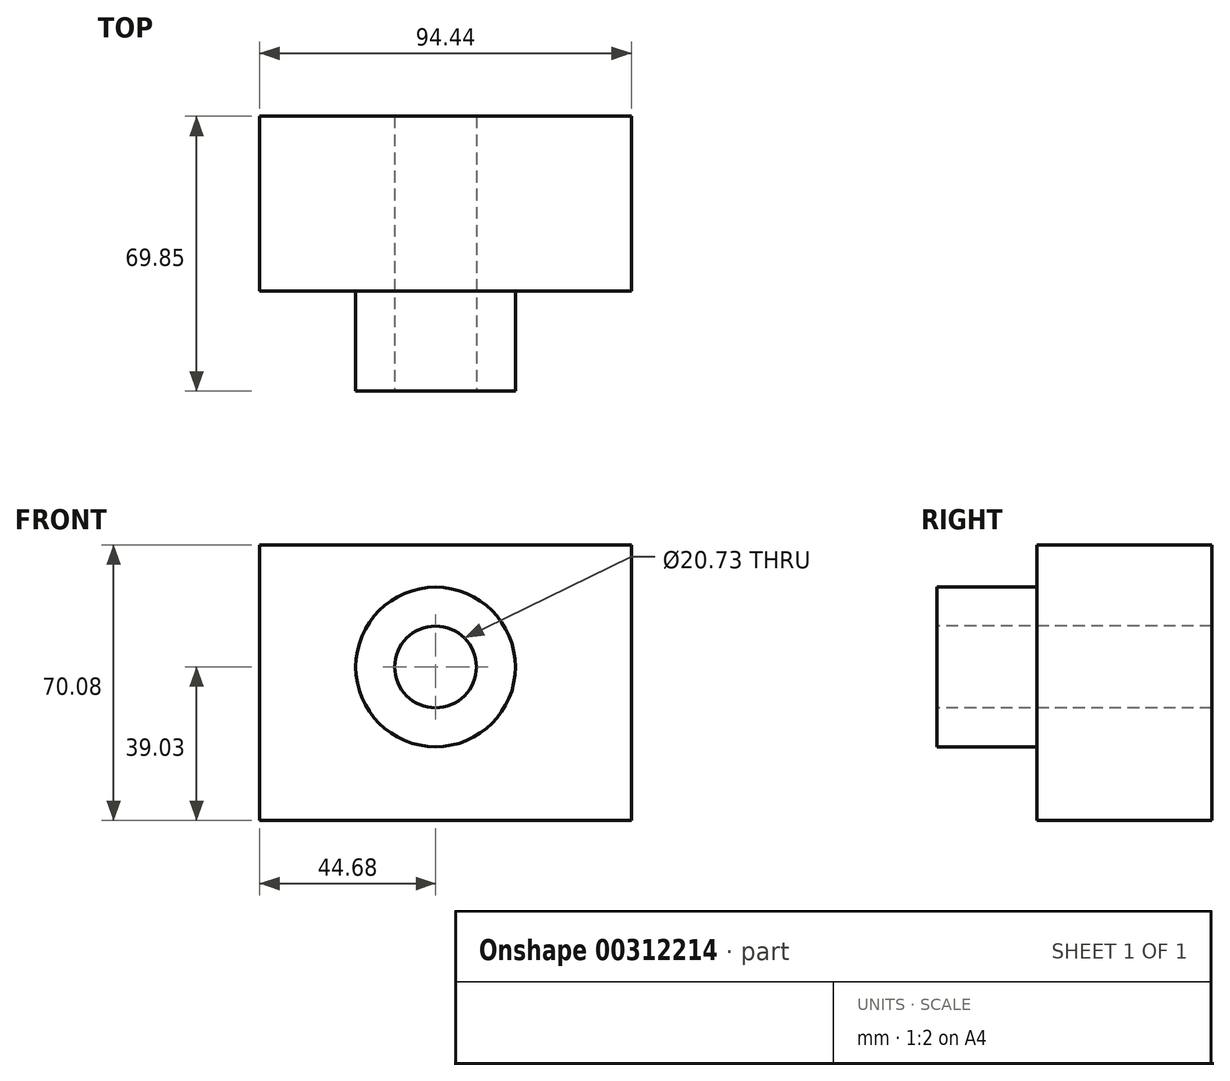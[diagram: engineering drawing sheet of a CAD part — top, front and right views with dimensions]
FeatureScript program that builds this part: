
annotation { "Feature Type Name" : "Feature", "Feature Type Description" : "" }
export const myFeature = defineFeature(function(context is Context, id is Id, definition is map)
    precondition{}
    {
        {
            var Q0;
            Q0=qCreatedBy(makeId("Front.planeOp"),FACE);
            var sketch = newSketch(context, id + "F0", { "sketchPlane" : qUnion([Q0])});
            skLineSegment(sketch, "E0.bottom", {"start": v(-44.68, 31.05) * mm, "end": v(49.76, 31.05) * mm});
            skLineSegment(sketch, "E0.top", {"start": v(-44.68, -39.03) * mm, "end": v(49.76, -39.03) * mm});
            skLineSegment(sketch, "E0.left", {"start": v(-44.68, 31.05) * mm, "end": v(-44.68, -39.03) * mm});
            skLineSegment(sketch, "E0.right", {"start": v(49.76, 31.05) * mm, "end": v(49.76, -39.03) * mm});
            skSolve(sketch);
        }
        {
            var Q0;
            Q0 = qSketchRegion(id + "F0", true);
            extrude(context, id + "F1", {"entities" : qUnion([Q0]), "depth" : 44.45 * mm});
        }
        {
            var Q0;
            Q0=makeQuery(id+"F1.opExtrude","CAP_FACE",FACE,{"disambiguationData":[OSD([sQuery(id+"F0.wireOp",EDGE,"E0.bottom"),sQuery(id+"F0.wireOp",EDGE,"E0.top"),sQuery(id+"F0.wireOp",EDGE,"E0.left"),sQuery(id+"F0.wireOp",EDGE,"E0.right")])],"isStart":false});
            var sketch = newSketch(context, id + "F2", { "sketchPlane" : qUnion([Q0])});
            skCircle(sketch, "E1", {"center": v(0, 0) * mm, "radius": 20.28 * mm});
            skSolve(sketch);
        }
        {
            var Q0;
            Q0=makeQuery(id+"F2.imprint","IMPRINT",FACE,{"disambiguationData":[TD([[makeQuery(id+"F2.imprint","IMPRINT",EDGE,{"derivedFrom":sQuery(id+"F2.wireOp",EDGE,"E1")}),1.0]])]});
            extrude(context, id + "F3", {"entities" : qUnion([Q0]), "operationType" : NewBodyOperationType.ADD, "depth" : 25.4 * mm});
        }
        {
            var Q0;
            Q0=makeQuery(id+"F3.opExtrude","CAP_FACE",FACE,{"disambiguationData":[OSD([sQuery(id+"F2.wireOp",EDGE,"E1")])],"isStart":false});
            var sketch = newSketch(context, id + "F4", { "sketchPlane" : qUnion([Q0])});
            skCircle(sketch, "E2", {"center": v(0, 0) * mm, "radius": 10.36 * mm});
            skSolve(sketch);
        }
        {
            var Q0;
            Q0 = qSketchRegion(id + "F4", true);
            extrude(context, id + "F5", {"entities" : qUnion([Q0]), "operationType" : NewBodyOperationType.REMOVE, "endBound" : BoundingType.UP_TO_NEXT, "oppositeDirection" : true, "depth" : 91.44 * mm});
        }
    });
